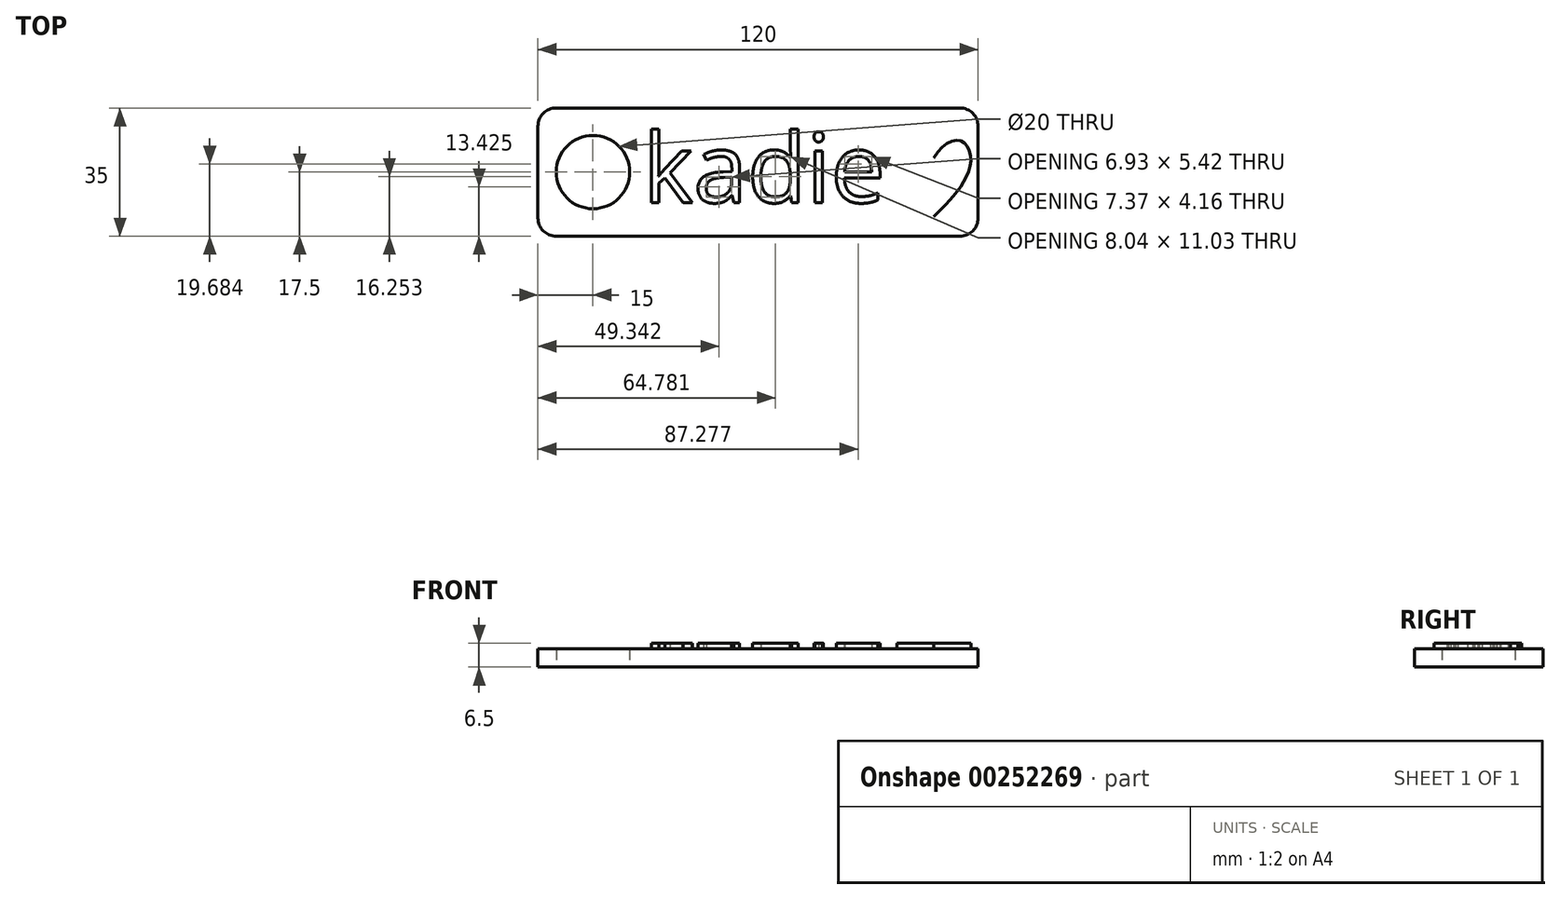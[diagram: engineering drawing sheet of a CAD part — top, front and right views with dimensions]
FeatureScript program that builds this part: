
annotation { "Feature Type Name" : "Feature", "Feature Type Description" : "" }
export const myFeature = defineFeature(function(context is Context, id is Id, definition is map)
    precondition{}
    {
        {
            var Q0;
            Q0=qCreatedBy(makeId("Top.planeOp"),FACE);
            var sketch = newSketch(context, id + "F0", { "sketchPlane" : qUnion([Q0])});
            skLineSegment(sketch, "E0.bottom", {"start": v(60, 17.5) * mm, "end": v(-60, 17.5) * mm});
            skLineSegment(sketch, "E0.top", {"start": v(60, -17.5) * mm, "end": v(-60, -17.5) * mm});
            skLineSegment(sketch, "E0.left", {"start": v(60, 17.5) * mm, "end": v(60, -17.5) * mm});
            skLineSegment(sketch, "E0.right", {"start": v(-60, 17.5) * mm, "end": v(-60, -17.5) * mm});
            skPoint(sketch, "E0.middle", {"position": v(0, 0) * mm});
            skCircle(sketch, "E1", {"center": v(-45, 0) * mm, "radius": 10 * mm});
            skSolve(sketch);
        }
        {
            var Q0;
            Q0 = qSketchRegion(id + "F0", true);
            extrude(context, id + "F1", {"entities" : qUnion([Q0]), "depth" : 5 * mm});
        }
        {
            var Q0;
            Q0=makeQuery(id+"F1.opExtrude","SWEPT_EDGE",EDGE,{"disambiguationData":[OSD([sQuery(id+"F0.wireOp",EDGE,"E0.top"),sQuery(id+"F0.wireOp",EDGE,"E0.left")])]});
            var Q1;
            Q1=makeQuery(id+"F1.opExtrude","SWEPT_EDGE",EDGE,{"disambiguationData":[OSD([sQuery(id+"F0.wireOp",EDGE,"E0.bottom"),sQuery(id+"F0.wireOp",EDGE,"E0.left")])]});
            var Q2;
            Q2=makeQuery(id+"F1.opExtrude","SWEPT_EDGE",EDGE,{"disambiguationData":[OSD([sQuery(id+"F0.wireOp",EDGE,"E0.bottom"),sQuery(id+"F0.wireOp",EDGE,"E0.right")])]});
            var Q3;
            Q3=makeQuery(id+"F1.opExtrude","SWEPT_EDGE",EDGE,{"disambiguationData":[OSD([sQuery(id+"F0.wireOp",EDGE,"E0.top"),sQuery(id+"F0.wireOp",EDGE,"E0.right")])]});
            fillet(context, id + "F2", {"entities" : qUnion([Q0, Q1, Q2, Q3]), "radius" : 5 * mm, "tangentPropagation" : true, "allowEdgeOverflow" : false});
        }
        {
            var Q0;
            Q0=makeQuery(id+"F1.opExtrude","CAP_FACE",FACE,{"disambiguationData":[OSD([sQuery(id+"F0.wireOp",EDGE,"E0.bottom"),sQuery(id+"F0.wireOp",EDGE,"E0.top"),sQuery(id+"F0.wireOp",EDGE,"E0.left"),sQuery(id+"F0.wireOp",EDGE,"E0.right"),sQuery(id+"F0.wireOp",EDGE,"E1")])],"isStart":false});
            var sketch = newSketch(context, id + "F3", { "sketchPlane" : qUnion([Q0])});
            skText(sketch, "E2", { "text": "kadie", "fontName": "OpenSans-Regular.ttf"});
            skLineSegment(sketch, "E3", {"start": v(47.96, 17.5) * mm, "end": v(47.96, -17.5) * mm, "construction": true});
            skFitSpline(sketch, "E4", {"points": [v(47.96, 3.85) * mm, v(40.86, 8.59) * mm, v(37.9, 3.55) * mm, v(41.45, -5.03) * mm, v(47.96, -12.14) * mm], "startDerivative": vector(-21.97, 40.93) * mm, "endDerivative": vector(25.72, -26.24) * mm});
            skFitSpline(sketch, "E5.MirrorCS", {"points": [v(47.96, 3.85) * mm, v(55.07, 8.59) * mm, v(58.03, 3.55) * mm, v(54.47, -5.03) * mm, v(47.96, -12.14) * mm], "startDerivative": vector(21.97, 40.93) * mm, "endDerivative": vector(-25.72, -26.24) * mm});
            const initialGuessF3  = {"E2": [-0.03138, -0.00829, 1, 0, 0.01895]};
            skSetInitialGuess(sketch, initialGuessF3);
            skSolve(sketch);
        }
        {
            var Q0;
            Q0 = qSketchRegion(id + "F3", true);
            extrude(context, id + "F4", {"entities" : qUnion([Q0]), "depth" : 1.5 * mm});
        }
    });
